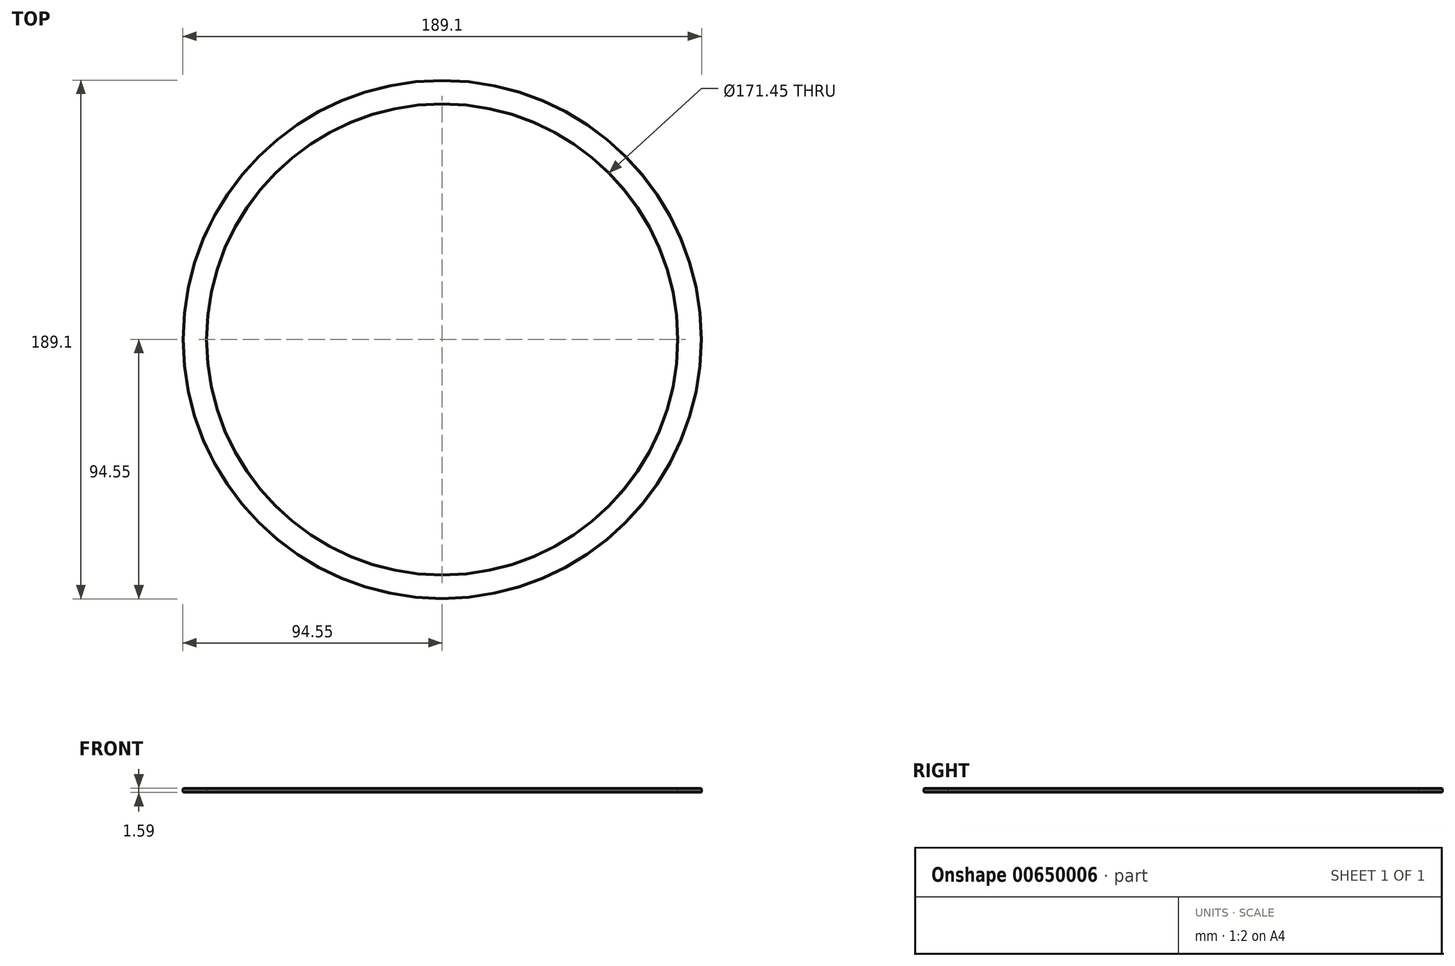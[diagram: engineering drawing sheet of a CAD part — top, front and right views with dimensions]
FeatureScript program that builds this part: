
annotation { "Feature Type Name" : "Feature", "Feature Type Description" : "" }
export const myFeature = defineFeature(function(context is Context, id is Id, definition is map)
    precondition{}
    {
        {
            var Q0;
            Q0=qCreatedBy(makeId("Top.planeOp"),FACE);
            var sketch = newSketch(context, id + "F0", { "sketchPlane" : qUnion([Q0])});
            skCircle(sketch, "E0", {"center": v(0, 0) * mm, "radius": 94.55 * mm});
            skCircle(sketch, "E1", {"center": v(0, 0) * mm, "radius": 85.73 * mm});
            skSolve(sketch);
        }
        {
            var Q0;
            Q0 = qSketchRegion(id + "F0", true);
            extrude(context, id + "F1", {"entities" : qUnion([Q0]), "depth" : 1.59 * mm, "offsetDistance" : 25.4 * mm});
        }
        {
            var Q0;
            Q0=makeQuery(id+"F1.opExtrude","CAP_EDGE",EDGE,{"disambiguationData":[OSD([sQuery(id+"F0.wireOp",EDGE,"E0")])],"isStart":false});
            var Q1;
            Q1=makeQuery(id+"F1.opExtrude","CAP_EDGE",EDGE,{"disambiguationData":[OSD([sQuery(id+"F0.wireOp",EDGE,"E1")])],"isStart":false});
            var Q2;
            Q2=makeQuery(id+"F1.opExtrude","CAP_EDGE",EDGE,{"disambiguationData":[OSD([sQuery(id+"F0.wireOp",EDGE,"E0")])],"isStart":true});
            var Q3;
            Q3=makeQuery(id+"F1.opExtrude","CAP_EDGE",EDGE,{"disambiguationData":[OSD([sQuery(id+"F0.wireOp",EDGE,"E1")])],"isStart":true});
            chamfer(context, id + "F2", {"entities" : qUnion([Q0, Q1, Q2, Q3]), "width" : 0.25 * mm, "tangentPropagation" : true});
        }
    });
